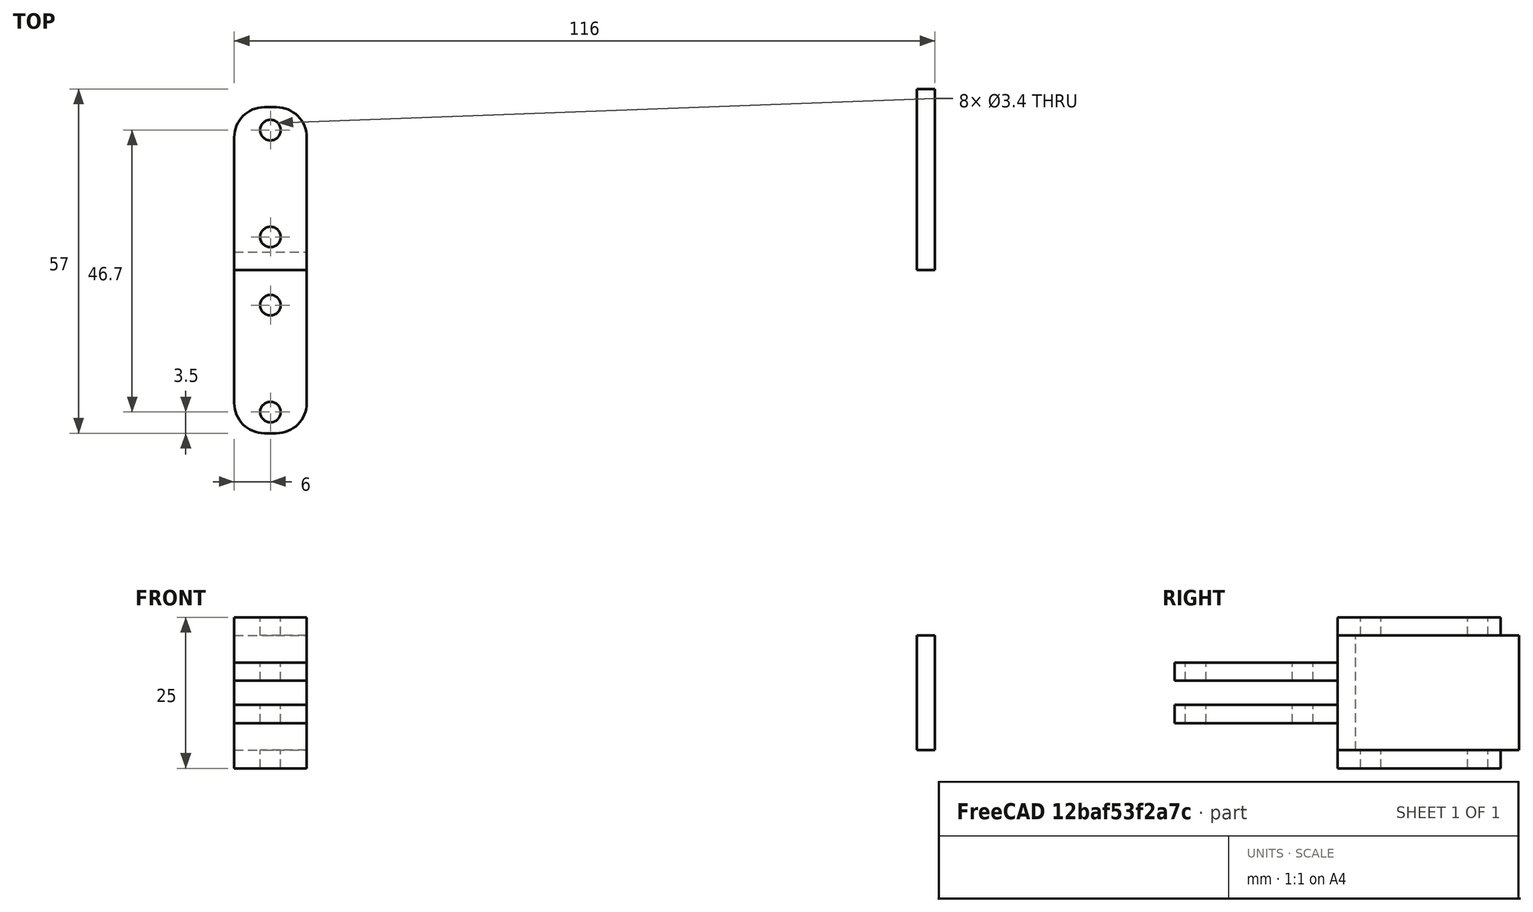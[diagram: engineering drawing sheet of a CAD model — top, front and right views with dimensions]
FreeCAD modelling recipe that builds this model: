
FCSTD DOCUMENT  (FreeCAD 0.15R4671 (Git))
Label: runner base2
License: CreativeCommons Attribution-ShareAlike
LicenseURL: http://creativecommons.org/licenses/by-sa/4.0/
objects: Part::Box×6, Part::MultiFuse×4, Part::Cylinder×2, Part::Cut×1, Part::Fillet×1
note: 14 computed .brp shape members not serialized (recipe doc carries the construction recipe); baked Part::Feature solids carry a one-line shape summary decoded from their .brp

FEATURE [Part::Box] Box  label="Cube"
  Height = 19
  Length = 12
  Width = 3
FEATURE [Part::Box] Box001  label="Cube001"
  Height = 3
  Length = 12
  Placement = pos=(0,0,-3) rot=(0,0,1;0rad)
  Width = 27
FEATURE [Part::Box] Box002  label="Cube002"
  Height = 3
  Length = 12
  Placement = pos=(0,0,19) rot=(0,0,1;0rad)
  Width = 27
FEATURE [Part::Box] Box003  label="Cube003"
  Height = 19
  Length = 3
  Placement = pos=(113,0,0) rot=(0,0,1;0rad)
  Width = 30
FEATURE [Part::Cylinder] Cylinder
  Angle = 360
  Height = 31
  Placement = pos=(6,5.5,-6) rot=(0,0,1;0rad)
  Radius = 1.7
FEATURE [Part::Cylinder] Cylinder001
  Angle = 360
  Height = 31
  Placement = pos=(6,23.2,-6) rot=(0,0,1;0rad)
  Radius = 1.7
FEATURE [Part::MultiFuse] Fusion001  label="orificios"
  Shapes = -> [Cylinder,Cylinder001]
FEATURE [Part::Box] Box004  label="Cube004"
  Height = 3
  Length = 12
  Placement = pos=(0,-27,4.5) rot=(0,0,1;0rad)
  Width = 27
FEATURE [Part::Box] Box005  label="Cube005"
  Height = 3
  Length = 12
  Placement = pos=(0,-27,11.5) rot=(0,0,1;0rad)
  Width = 27
FEATURE [Part::MultiFuse] Fusion  label="orificios001"
  Placement = pos=(0,-29,0) rot=(0,0,1;0rad)
  Shapes = -> [Cylinder,Cylinder001]
FEATURE [Part::MultiFuse] Fusion002  label="orificios todos"
  Shapes = -> [Fusion001,Fusion]
FEATURE [Part::MultiFuse] Fusion003  label="cuerpo"
  Shapes = -> [Box,Box001,Box002,Box004,Box005]
FEATURE [Part::Cut] Cut
  Base = -> Fusion003
  Tool = -> Fusion002
FEATURE [Part::Fillet] Fillet
  Base = -> Cut
  Edges = 8 edges r=5: [Edge2,Edge4,Edge12,Edge17,Edge21,Edge33,Edge37,Edge42]
